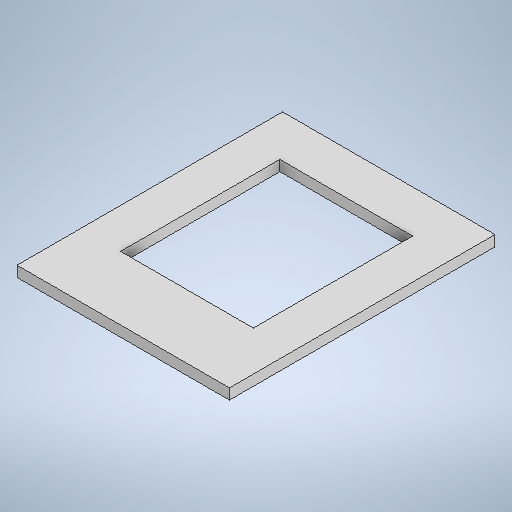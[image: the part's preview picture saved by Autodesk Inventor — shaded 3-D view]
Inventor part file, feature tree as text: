
AUTODESK INVENTOR PART (.ipt)
format: ipt  version: 2025.1 (Build 291241000, 241)  size: 241,152 bytes
history: native  units: mm
features: extrude x2, sketch x2
ambient origin geometry x8: Origin, YZ Plane, XZ Plane, XY Plane, X Axis, Y Axis, Z Axis, Center Point
bodies: Volumenkörper1 (feature_tree)
feature tree (4):
  extrude  "Extrusion1"  Depth=500.0mm
  extrude  "Extrusion2"  Depth=300.0mm
  sketch  "Skizze1"  dims[d0=400.0mm d1=500.0mm]
  sketch  "Skizze2"  dims[d2=20.0mm d3=0.0mm d4=300.0mm d5=250.0mm d6=80.0mm d7=20.0mm d8=0.0mm]
